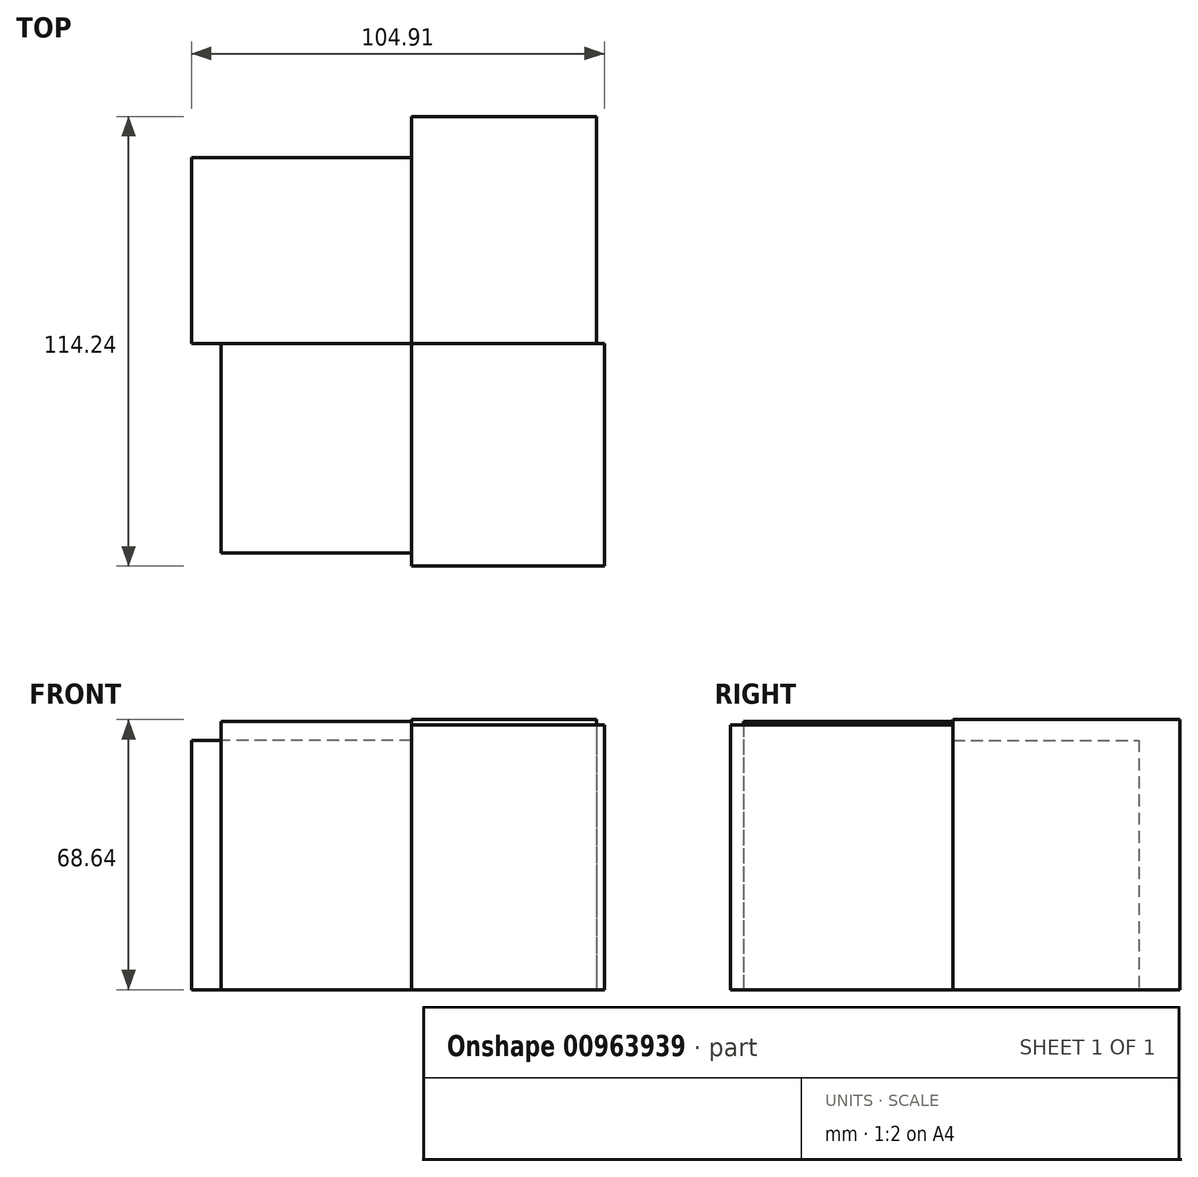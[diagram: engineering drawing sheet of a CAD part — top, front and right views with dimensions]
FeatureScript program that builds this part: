
annotation { "Feature Type Name" : "Feature", "Feature Type Description" : "" }
export const myFeature = defineFeature(function(context is Context, id is Id, definition is map)
    precondition{}
    {
        {
            var Q0;
            Q0=qCreatedBy(makeId("Top.planeOp"),FACE);
            var sketch = newSketch(context, id + "F0", { "sketchPlane" : qUnion([Q0])});
            skCircle(sketch, "E0", {"center": v(0, 0) * mm, "radius": 75.52 * mm});
            skSolve(sketch);
        }
        {
            var Q0;
            Q0=sQuery(id+"F0.wireOp",EDGE,"E0");
            extrude(context, id + "F1", {"bodyType" : ToolBodyType.SURFACE, "surfaceEntities" : qUnion([Q0]), "depth" : 72 * mm, "offsetDistance" : 25.4 * mm});
        }
        {
            var Q0;
            Q0=qCreatedBy(makeId("Top.planeOp"),FACE);
            var sketch = newSketch(context, id + "F2", { "sketchPlane" : qUnion([Q0])});
            skLineSegment(sketch, "E1.bottom", {"start": v(0, 0) * mm, "end": v(-55.87, 0) * mm});
            skLineSegment(sketch, "E1.top", {"start": v(0, 47.2) * mm, "end": v(-55.87, 47.2) * mm});
            skLineSegment(sketch, "E1.left", {"start": v(0, 0) * mm, "end": v(0, 47.2) * mm});
            skLineSegment(sketch, "E1.right", {"start": v(-55.87, 0) * mm, "end": v(-55.87, 47.2) * mm});
            skSolve(sketch);
        }
        {
            var Q0;
            Q0 = qSketchRegion(id + "F2", true);
            extrude(context, id + "F3", {"entities" : qUnion([Q0]), "depth" : 63.35 * mm, "offsetDistance" : 25.4 * mm});
        }
        {
            var Q0;
            Q0=qCreatedBy(makeId("Top.planeOp"),FACE);
            var sketch = newSketch(context, id + "F4", { "sketchPlane" : qUnion([Q0])});
            skLineSegment(sketch, "E2.bottom", {"start": v(0, 0) * mm, "end": v(49.04, 0) * mm});
            skLineSegment(sketch, "E2.top", {"start": v(0, -56.55) * mm, "end": v(49.04, -56.55) * mm});
            skLineSegment(sketch, "E2.left", {"start": v(0, 0) * mm, "end": v(0, -56.55) * mm});
            skLineSegment(sketch, "E2.right", {"start": v(49.04, 0) * mm, "end": v(49.04, -56.55) * mm});
            skSolve(sketch);
        }
        {
            var Q0;
            Q0=makeQuery(id+"F4.imprint","IMPRINT",FACE,{"disambiguationData":[TD([[makeQuery(id+"F4.imprint","IMPRINT",EDGE,{"derivedFrom":sQuery(id+"F4.wireOp",EDGE,"E2.bottom")}),-1.0]])]});
            extrude(context, id + "F5", {"entities" : qUnion([Q0]), "depth" : 67.24 * mm, "offsetDistance" : 25.4 * mm});
        }
        {
            var Q0;
            Q0=qCreatedBy(makeId("Top.planeOp"),FACE);
            var sketch = newSketch(context, id + "F6", { "sketchPlane" : qUnion([Q0])});
            skLineSegment(sketch, "E3.bottom", {"start": v(0, 0) * mm, "end": v(47.08, 0) * mm});
            skLineSegment(sketch, "E3.top", {"start": v(0, 57.7) * mm, "end": v(47.08, 57.7) * mm});
            skLineSegment(sketch, "E3.left", {"start": v(0, 0) * mm, "end": v(0, 57.7) * mm});
            skLineSegment(sketch, "E3.right", {"start": v(47.08, 0) * mm, "end": v(47.08, 57.7) * mm});
            skSolve(sketch);
        }
        {
            var Q0;
            Q0=makeQuery(id+"F6.imprint","IMPRINT",FACE,{"disambiguationData":[TD([[makeQuery(id+"F6.imprint","IMPRINT",EDGE,{"derivedFrom":sQuery(id+"F6.wireOp",EDGE,"E3.bottom")}),1.0]])]});
            extrude(context, id + "F7", {"entities" : qUnion([Q0]), "depth" : 68.64 * mm, "offsetDistance" : 25.4 * mm});
        }
        {
            var Q0;
            Q0=qCreatedBy(makeId("Top.planeOp"),FACE);
            var sketch = newSketch(context, id + "F8", { "sketchPlane" : qUnion([Q0])});
            skLineSegment(sketch, "E4.bottom", {"start": v(0, 0) * mm, "end": v(-48.3, 0) * mm});
            skLineSegment(sketch, "E4.top", {"start": v(0, -53.18) * mm, "end": v(-48.3, -53.18) * mm});
            skLineSegment(sketch, "E4.left", {"start": v(0, 0) * mm, "end": v(0, -53.18) * mm});
            skLineSegment(sketch, "E4.right", {"start": v(-48.3, 0) * mm, "end": v(-48.3, -53.18) * mm});
            skSolve(sketch);
        }
        {
            var Q0;
            Q0 = qSketchRegion(id + "F8", true);
            extrude(context, id + "F9", {"entities" : qUnion([Q0]), "depth" : 68.14 * mm, "offsetDistance" : 25.4 * mm});
        }
    });
